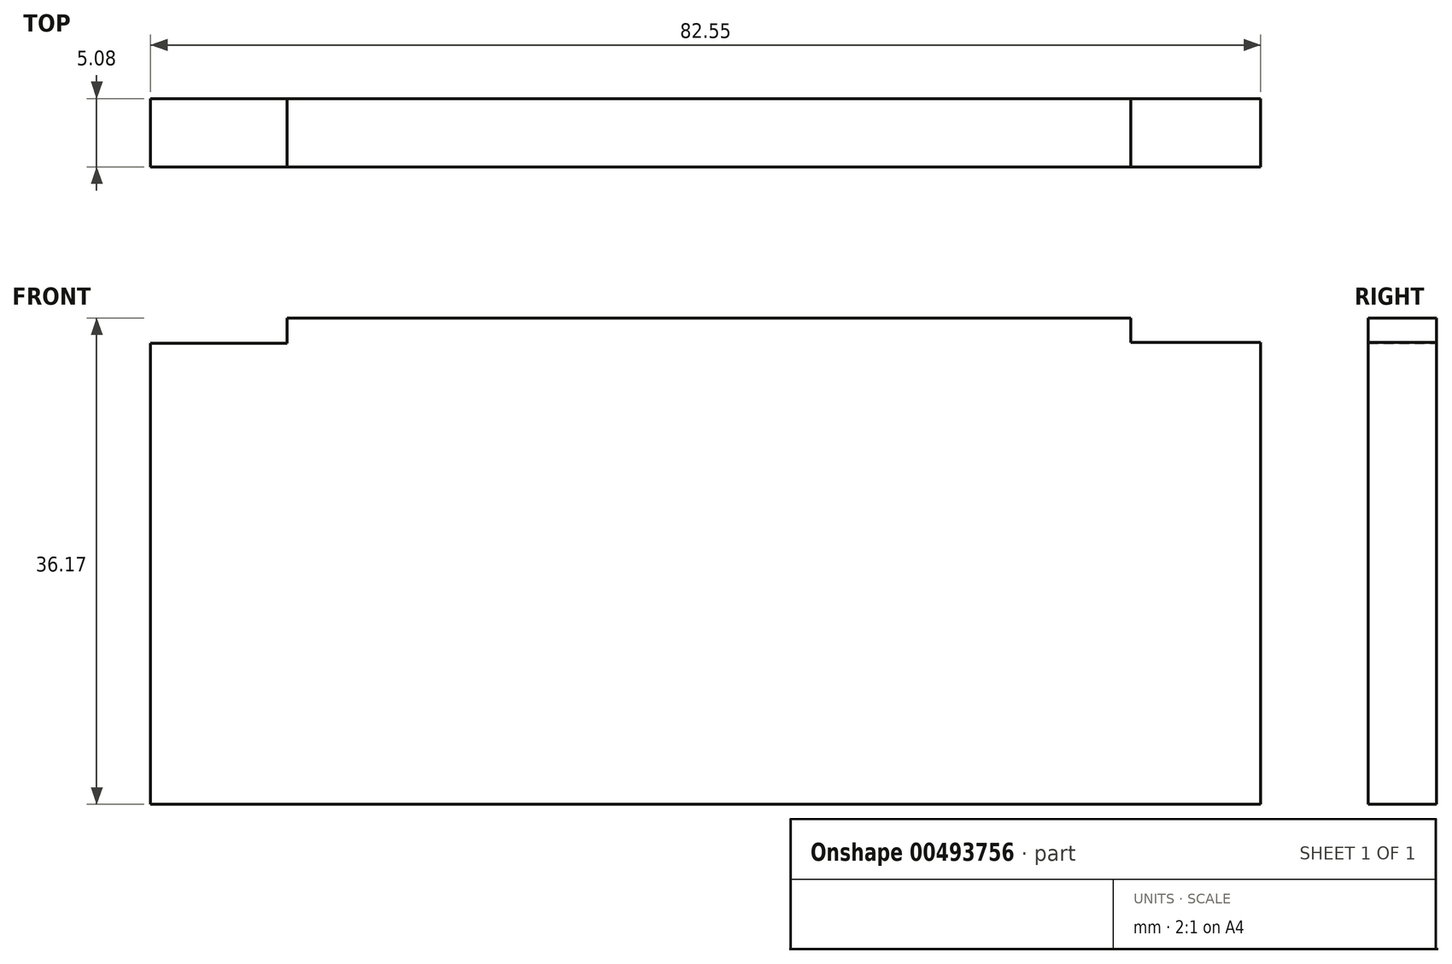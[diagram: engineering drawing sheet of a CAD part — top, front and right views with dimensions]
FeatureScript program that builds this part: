
annotation { "Feature Type Name" : "Feature", "Feature Type Description" : "" }
export const myFeature = defineFeature(function(context is Context, id is Id, definition is map)
    precondition{}
    {
        {
            var Q0;
            Q0=qCreatedBy(makeId("Front.planeOp"),FACE);
            var sketch = newSketch(context, id + "F0", { "sketchPlane" : qUnion([Q0])});
            skLineSegment(sketch, "E0.bottom", {"start": v(-20.46, 13) * mm, "end": v(42.28, 13) * mm});
            skLineSegment(sketch, "E0.top", {"start": v(-30.62, -23.18) * mm, "end": v(51.93, -23.18) * mm});
            skLineSegment(sketch, "E0.left", {"start": v(-30.62, 11.13) * mm, "end": v(-30.62, -23.18) * mm});
            skLineSegment(sketch, "E0.right", {"start": v(51.93, 11.17) * mm, "end": v(51.93, -23.18) * mm});
            skLineSegment(sketch, "E1.top", {"start": v(-30.62, 11.13) * mm, "end": v(-20.46, 11.13) * mm});
            skLineSegment(sketch, "E1.right", {"start": v(-20.46, 12.9) * mm, "end": v(-20.46, 11.13) * mm});
            skLineSegment(sketch, "E2.top", {"start": v(42.28, 11.17) * mm, "end": v(51.93, 11.17) * mm});
            skLineSegment(sketch, "E2.left", {"start": v(42.28, 12.95) * mm, "end": v(42.28, 11.17) * mm});
            skLineSegment(sketch, "E3", {"start": v(-20.46, 13) * mm, "end": v(-20.46, 12.9) * mm});
            skLineSegment(sketch, "E4", {"start": v(42.28, 13) * mm, "end": v(42.28, 12.95) * mm});
            skSolve(sketch);
        }
        {
            var Q0;
            Q0=qSketchRegion(id+"F0",true);
            extrude(context, id + "F1", {"entities" : qUnion([Q0]), "depth" : 5.08 * mm});
        }
    });
